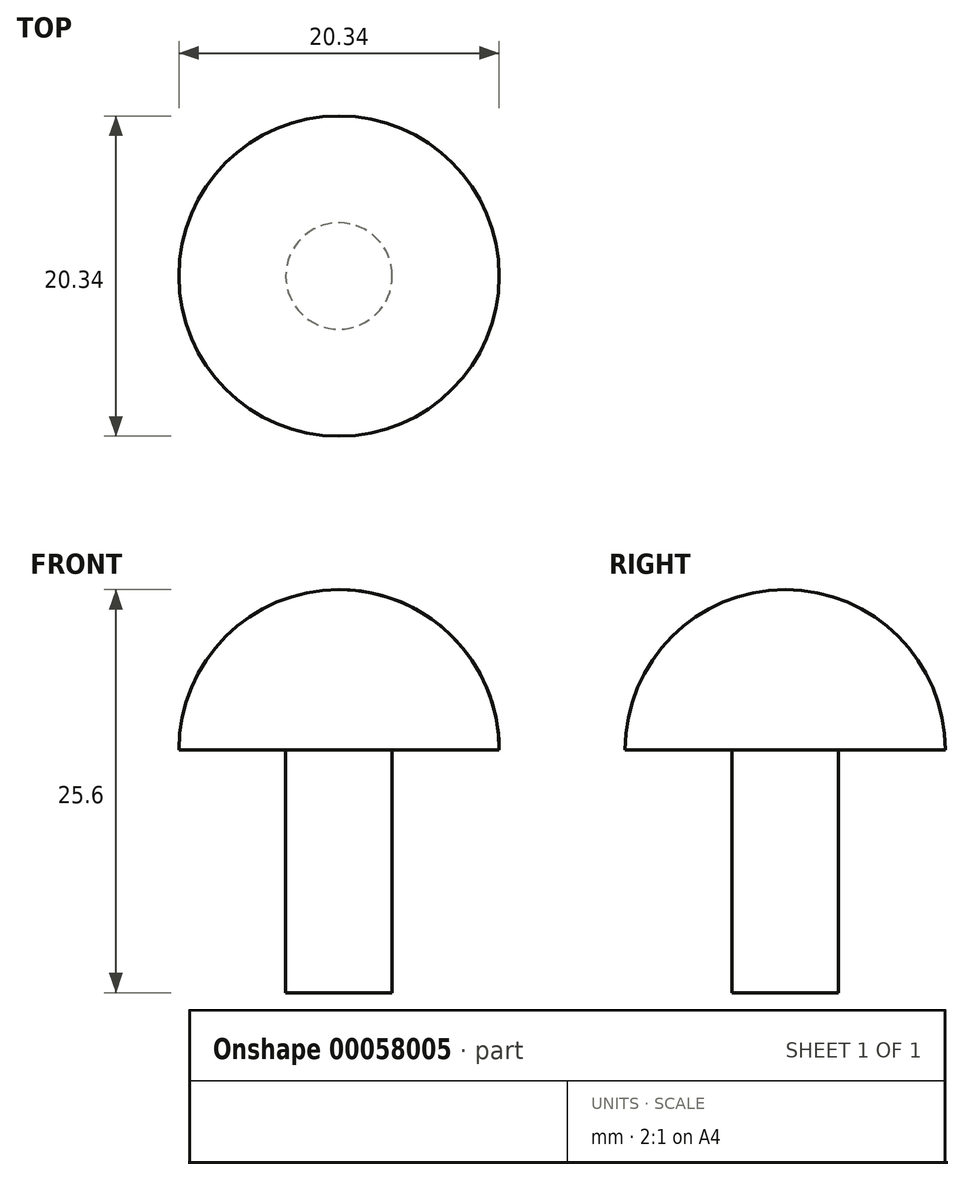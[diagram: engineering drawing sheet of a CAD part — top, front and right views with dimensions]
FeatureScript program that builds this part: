
annotation { "Feature Type Name" : "Feature", "Feature Type Description" : "" }
export const myFeature = defineFeature(function(context is Context, id is Id, definition is map)
    precondition{}
    {
        {
            var Q0;
            Q0=qCreatedBy(makeId("Front.planeOp"),FACE);
            var sketch = newSketch(context, id + "F0", { "sketchPlane" : qUnion([Q0])});
            skArc(sketch, "E0", {"start": v(10.17, 0) * mm, "mid": v(7.2, 7.2) * mm, "end": v(0, 10.17) * mm});
            skLineSegment(sketch, "E1.bottom", {"start": v(0, -15.43) * mm, "end": v(3.38, -15.43) * mm});
            skLineSegment(sketch, "E1.left", {"start": v(0, -15.43) * mm, "end": v(0, 0) * mm});
            skLineSegment(sketch, "E1.right", {"start": v(3.38, -15.43) * mm, "end": v(3.38, 0) * mm});
            skLineSegment(sketch, "E2", {"start": v(0, 0) * mm, "end": v(0, 10.17) * mm});
            skLineSegment(sketch, "E3", {"start": v(3.38, 0) * mm, "end": v(10.17, 0) * mm});
            skSolve(sketch);
        }
        {
            var Q0;
            Q0=makeQuery(id+"F0.imprint","IMPRINT",FACE,{"disambiguationData":[TD([[makeQuery(id+"F0.imprint","IMPRINT",EDGE,{"derivedFrom":sQuery(id+"F0.wireOp",EDGE,"E0")}),1.0]])]});
            var Q1;
            Q1=sQuery(id+"F0.wireOp",EDGE,"E2");
            revolve(context, id + "F1", {"entities" : qUnion([Q0]), "axis" : qUnion([Q1]), "revolveType" : RevolveType.FULL});
        }
    });
